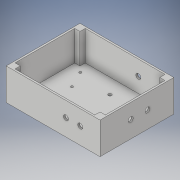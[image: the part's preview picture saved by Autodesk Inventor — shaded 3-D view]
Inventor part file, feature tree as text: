
AUTODESK INVENTOR PART (.ipt)
format: ipt  version: 2018 (Build 220112000, 112)  size: 196,608 bytes
history: native  units: in
note: dims shown in document units (in); Inventor stores cm internally (conversion verified against a paired STEP export)
features: extrude x7, sketch x7
ambient origin geometry x8: Origin, YZ Plane, XZ Plane, XY Plane, X Axis, Y Axis, Z Axis, Center Point
bodies: Solid1 (feature_tree)
feature tree (14):
  extrude  "Extrusion1"  Depth=3.701in
  extrude  "Extrusion2"  Depth=4.527in
  extrude  "Extrusion3"  Depth=0.354in
  sketch  "Sketch7"  dims[d7=0.354in d10=0.354in]
  extrude  "Extrusion7"  Depth=0.354in
  extrude  "Extrusion8"  Depth=1.5in TaperAngle=0.0deg
  extrude  "Extrusion9"  Depth=0.164in
  extrude  "Extrusion10"  Depth=3.543in
  sketch  "Sketch1"  dims[d0=4.705in d1=3.701in]
  sketch  "Sketch2"  dims[d2=0.089in d3=0.0in d4=4.527in]
  sketch  "Sketch3"  dims[d5=3.523in d6=0.354in]
  sketch  "Sketch8"  dims[d11=0.354in d14=1.5in d15=0.0in]
  sketch  "Sketch10"  dims[d18=0.164in d19=0.164in]
  sketch  "Sketch11"  dims[d20=0.0in d21=0.0in d47=3.543in d48=2.559in d62=2.598in d63=0.787in d64=0.118in d65=0.118in d66=0.118in d67=0.118in d72=1.0in d73=0.0in d78=0.0in d79=0.0in d80=0.227in d85=0.0in d86=0.0in d99=0.25in d112=0.25in d113=0.25in d118=0.25in d119=0.25in d120=3.5in d121=2.5313in d124=0.12in d127=0.12in d130=0.12in d131=0.04in d132=0.04in d133=0.12in d134=0.0in d135=0.0in]
